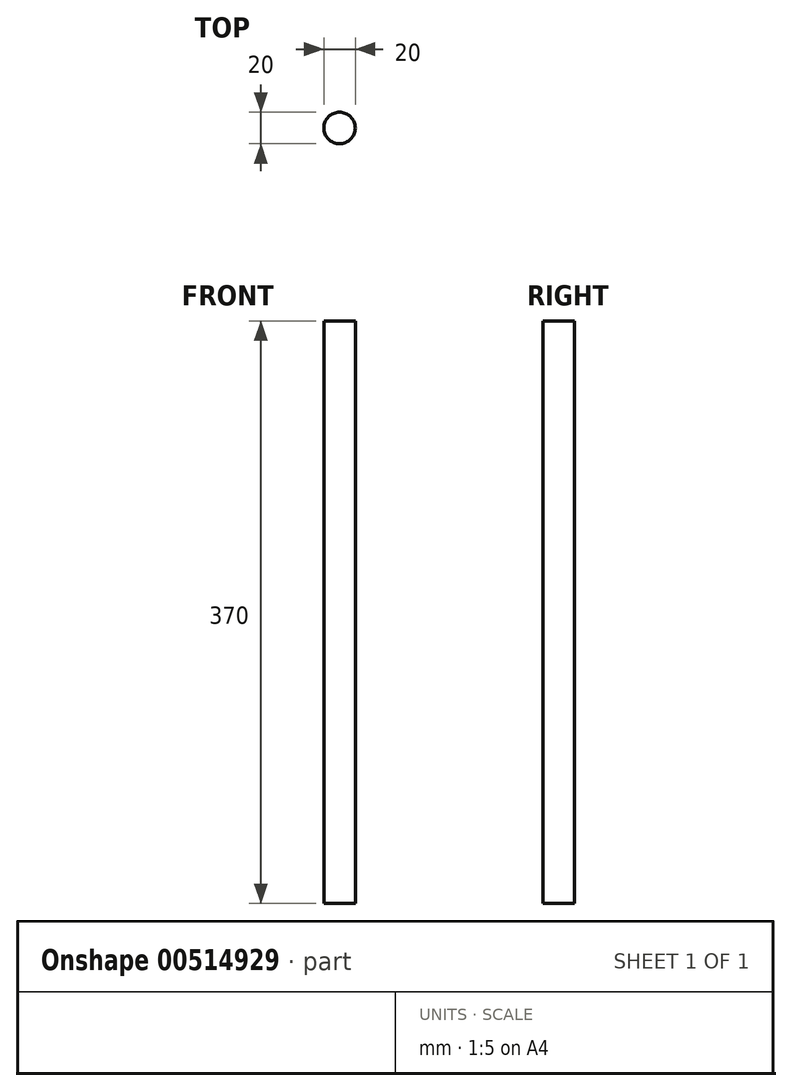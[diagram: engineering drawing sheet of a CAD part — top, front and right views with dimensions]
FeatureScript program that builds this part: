
annotation { "Feature Type Name" : "Feature", "Feature Type Description" : "" }
export const myFeature = defineFeature(function(context is Context, id is Id, definition is map)
    precondition{}
    {
        {
            var Q0;
            Q0=qCreatedBy(makeId("Top.planeOp"),FACE);
            var sketch = newSketch(context, id + "F0", { "sketchPlane" : qUnion([Q0])});
            skCircle(sketch, "E0", {"center": v(0, 0) * mm, "radius": 10 * mm});
            skSolve(sketch);
        }
        {
            var Q0;
            Q0=makeQuery(id+"F0.imprint","IMPRINT",FACE,{"disambiguationData":[TD([[makeQuery(id+"F0.imprint","IMPRINT",EDGE,{"derivedFrom":sQuery(id+"F0.wireOp",EDGE,"E0")}),1.0]])]});
            extrude(context, id + "F1", {"entities" : qUnion([Q0]), "endBound" : BoundingType.SYMMETRIC, "depth" : 370 * mm, "offsetDistance" : 25 * mm});
        }
    });
